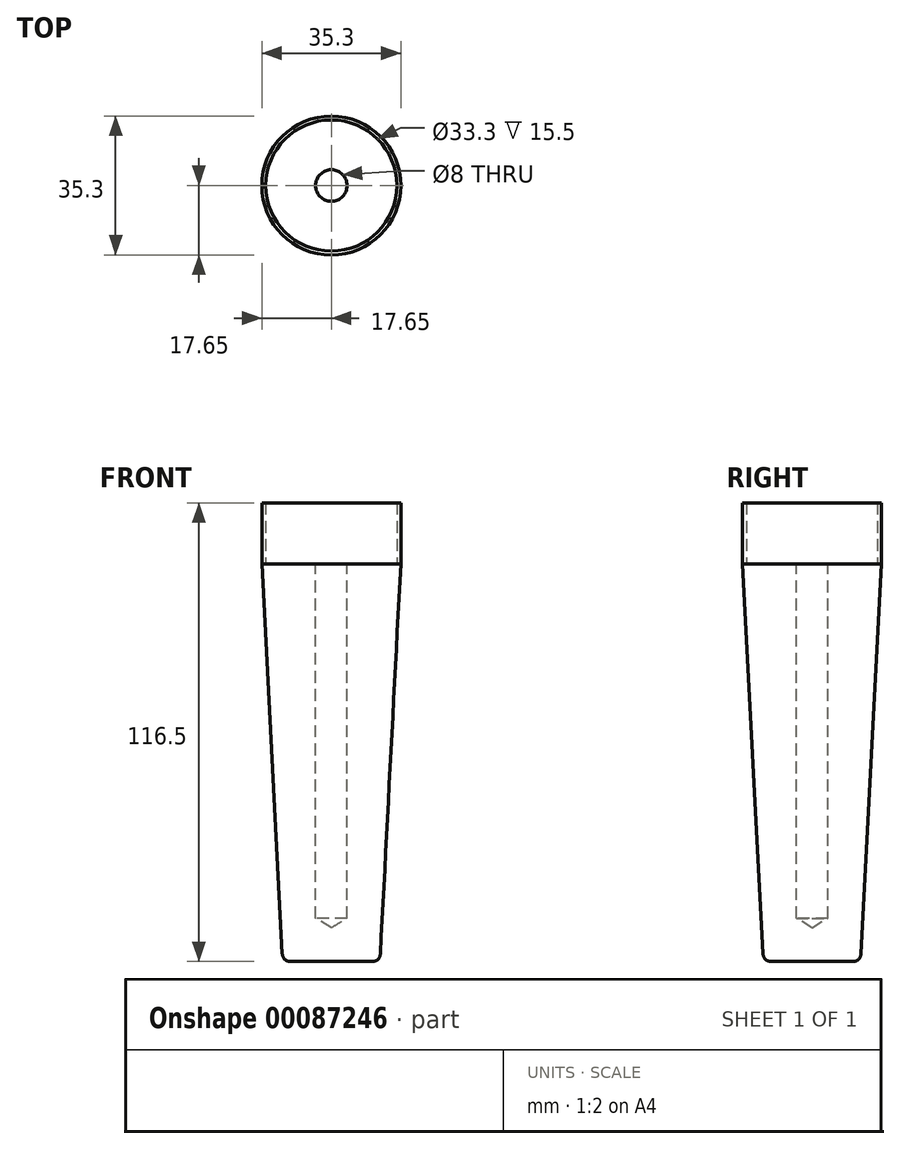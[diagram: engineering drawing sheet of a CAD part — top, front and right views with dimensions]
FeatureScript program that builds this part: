
annotation { "Feature Type Name" : "Feature", "Feature Type Description" : "" }
export const myFeature = defineFeature(function(context is Context, id is Id, definition is map)
    precondition{}
    {
        {
            var Q0;
            Q0=qCreatedBy(makeId("Top.planeOp"),FACE);
            var sketch = newSketch(context, id + "F0", { "sketchPlane" : qUnion([Q0])});
            skCircle(sketch, "E0", {"center": v(0, 0) * mm, "radius": 16.65 * mm});
            skCircle(sketch, "E1.0", {"center": v(0, 0) * mm, "radius": 17.65 * mm});
            skSolve(sketch);
        }
        {
            var Q0;
            Q0 = qSketchRegion(id + "F0", true);
            extrude(context, id + "F1", {"entities" : qUnion([Q0]), "depth" : 15.5 * mm});
        }
        {
            var Q0;
            Q0=makeQuery(id+"F0.imprint","IMPRINT",FACE,{"disambiguationData":[TD([[makeQuery(id+"F0.imprint","IMPRINT",EDGE,{"derivedFrom":sQuery(id+"F0.wireOp",EDGE,"E0")}),1.0]])]});
            var Q1;
            Q1=makeQuery(id+"F0.imprint","IMPRINT",FACE,{"disambiguationData":[TD([[makeQuery(id+"F0.imprint","IMPRINT",EDGE,{"derivedFrom":sQuery(id+"F0.wireOp",EDGE,"E0")}),-1.0]])]});
            extrude(context, id + "F2", {"entities" : qUnion([Q0, Q1]), "operationType" : NewBodyOperationType.ADD, "oppositeDirection" : true, "depth" : 101 * mm, "hasDraft" : true, "draftAngle" : 3 * degree, "draftPullDirection" : true});
        }
        {
            var Q0;
            Q0=makeQuery(id+"F2.opExtrude","CAP_EDGE",EDGE,{"disambiguationData":[OSD([sQuery(id+"F0.wireOp",EDGE,"E1.0")])],"isStart":false});
            fillet(context, id + "F3", {"entities" : qUnion([Q0]), "radius" : 2 * mm, "tangentPropagation" : true, "allowEdgeOverflow" : false});
        }
        {
            var Q0;
            Q0=sQuery(id+"F0.wireOp",VERTEX,"E0.center");
            var Q1;
            Q1=makeQuery(id+"F1.opExtrude","SWEPT_BODY",BODY,{"disambiguationData":[OSD([sQuery(id+"F0.wireOp",EDGE,"E0"),sQuery(id+"F0.wireOp",EDGE,"E1.0")])]});
            hole(context, id + "F4", {"style" : HoleStyle.SIMPLE, "endStyle" : HoleEndStyle.BLIND, "holeDiameter" : 8 * mm, "holeDepth" : 90 * mm, "locations" : qUnion([Q0]), "scope" : qUnion([Q1])});
        }
    });
